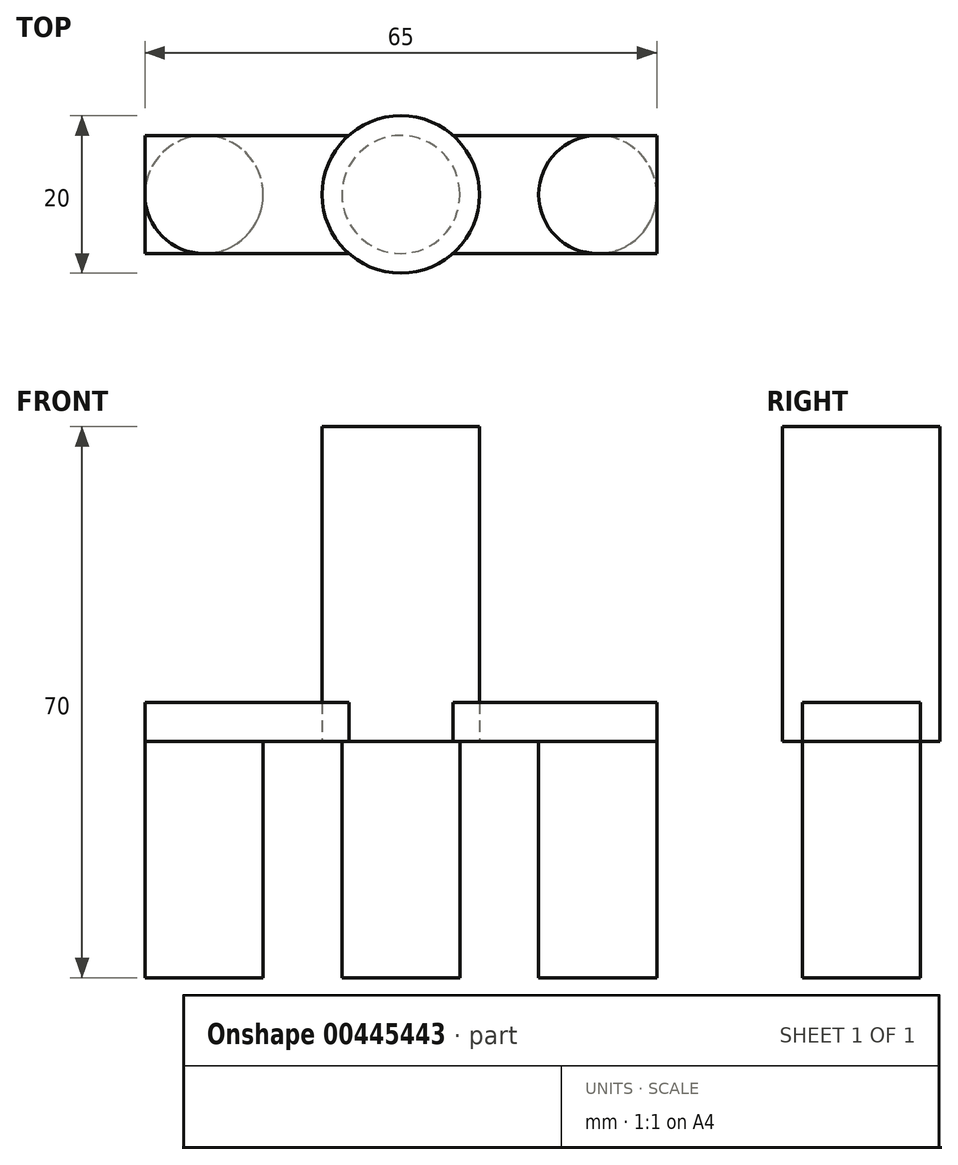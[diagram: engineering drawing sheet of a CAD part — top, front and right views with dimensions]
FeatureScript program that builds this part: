
annotation { "Feature Type Name" : "Feature", "Feature Type Description" : "" }
export const myFeature = defineFeature(function(context is Context, id is Id, definition is map)
    precondition{}
    {
        {
            var Q0;
            Q0=qCreatedBy(makeId("Top.planeOp"),FACE);
            var sketch = newSketch(context, id + "F0", { "sketchPlane" : qUnion([Q0])});
            skCircle(sketch, "E0", {"center": v(0, 0) * mm, "radius": 10 * mm});
            skLineSegment(sketch, "E1.bottom", {"start": v(32.5, 7.5) * mm, "end": v(-32.5, 7.5) * mm});
            skLineSegment(sketch, "E1.top", {"start": v(32.5, -7.5) * mm, "end": v(-32.5, -7.5) * mm});
            skLineSegment(sketch, "E1.left", {"start": v(32.5, 7.5) * mm, "end": v(32.5, -7.5) * mm});
            skLineSegment(sketch, "E1.right", {"start": v(-32.5, 7.5) * mm, "end": v(-32.5, -7.5) * mm});
            skSolve(sketch);
        }
        {
            var Q0;
            {var subQ5=sQuery(id+"F0.wireOp",EDGE,"E1.left");Q0=makeQuery(id+"F0.imprint","IMPRINT",FACE,{"disambiguationData":[TD([[makeQuery(id+"F0.imprint","IMPRINT",EDGE,{"derivedFrom":subQ5}),-1.0]])]});}
            var Q1;
            {var subQ5=sQuery(id+"F0.wireOp",EDGE,"E1.right");Q1=makeQuery(id+"F0.imprint","IMPRINT",FACE,{"disambiguationData":[TD([[makeQuery(id+"F0.imprint","IMPRINT",EDGE,{"derivedFrom":subQ5}),1.0]])]});}
            extrude(context, id + "F1", {"entities" : qUnion([Q0, Q1]), "depth" : 5 * mm});
        }
        {
            var Q0;
            Q0=qCreatedBy(makeId("Top.planeOp"),FACE);
            var sketch = newSketch(context, id + "F2", { "sketchPlane" : qUnion([Q0])});
            skCircle(sketch, "E2", {"center": v(0, 0) * mm, "radius": 10 * mm});
            skSolve(sketch);
        }
        {
            var Q0;
            Q0=makeQuery(id+"F2.imprint","IMPRINT",FACE,{"disambiguationData":[TD([[makeQuery(id+"F2.imprint","IMPRINT",EDGE,{"derivedFrom":sQuery(id+"F2.wireOp",EDGE,"E2")}),1.0]])]});
            extrude(context, id + "F3", {"entities" : qUnion([Q0]), "depth" : 40 * mm});
        }
        {
            var Q0;
            Q0=makeQuery(id+"F1.opExtrude","CAP_FACE",FACE,{"disambiguationData":[OSD([sQuery(id+"F0.wireOp",EDGE,"E0"),sQuery(id+"F0.wireOp",EDGE,"E1.bottom"),sQuery(id+"F0.wireOp",EDGE,"E1.top"),sQuery(id+"F0.wireOp",EDGE,"E1.right")])],"isStart":true});
            var sketch = newSketch(context, id + "F4", { "sketchPlane" : qUnion([Q0])});
            skCircle(sketch, "E3", {"center": v(0, 0) * mm, "radius": 7.5 * mm});
            skSolve(sketch);
        }
        {
            var Q0;
            Q0=makeQuery(id+"F4.imprint","IMPRINT",FACE,{"disambiguationData":[TD([[makeQuery(id+"F4.imprint","IMPRINT",EDGE,{"derivedFrom":sQuery(id+"F4.wireOp",EDGE,"E3")}),1.0]])]});
            extrude(context, id + "F5", {"entities" : qUnion([Q0]), "operationType" : NewBodyOperationType.ADD, "depth" : 30 * mm});
        }
        {
            var Q0;
            Q0=makeQuery(id+"F1.opExtrude","CAP_FACE",FACE,{"disambiguationData":[OSD([sQuery(id+"F0.wireOp",EDGE,"E0"),sQuery(id+"F0.wireOp",EDGE,"E1.bottom"),sQuery(id+"F0.wireOp",EDGE,"E1.top"),sQuery(id+"F0.wireOp",EDGE,"E1.right")])],"isStart":true});
            var sketch = newSketch(context, id + "F6", { "sketchPlane" : qUnion([Q0])});
            skCircle(sketch, "E4", {"center": v(-25, 0) * mm, "radius": 7.5 * mm});
            skCircle(sketch, "E5", {"center": v(25, 0) * mm, "radius": 7.5 * mm});
            skSolve(sketch);
        }
        {
            var Q0;
            {var subQ0=sQuery(id+"F6.wireOp",EDGE,"E4");var subQ1=sQuery(id+"F0.wireOp",EDGE,"E1.right");var subQ2=makeQuery(id+"F6.imprint","INTERSECT",VERTEX,{"derivedFrom":[makeQuery(id+"F1.opExtrude","CAP_EDGE",EDGE,{"disambiguationData":[OSD([subQ1])],"isStart":true}),subQ0]});Q0=makeQuery(id+"F6.imprint","IMPRINT",FACE,{"disambiguationData":[TD([[makeQuery(id+"F6.imprint","IMPRINT",EDGE,{"disambiguationData":[TD([[subQ2,1.0]])],"derivedFrom":subQ0}),1.0]])]});}
            var Q1;
            Q1=makeQuery(id+"F6.imprint","IMPRINT",FACE,{"disambiguationData":[TD([[makeQuery(id+"F6.imprint","IMPRINT",EDGE,{"derivedFrom":sQuery(id+"F6.wireOp",EDGE,"E5")}),1.0]])]});
            extrude(context, id + "F7", {"entities" : qUnion([Q0, Q1]), "depth" : 30 * mm});
        }
    });
